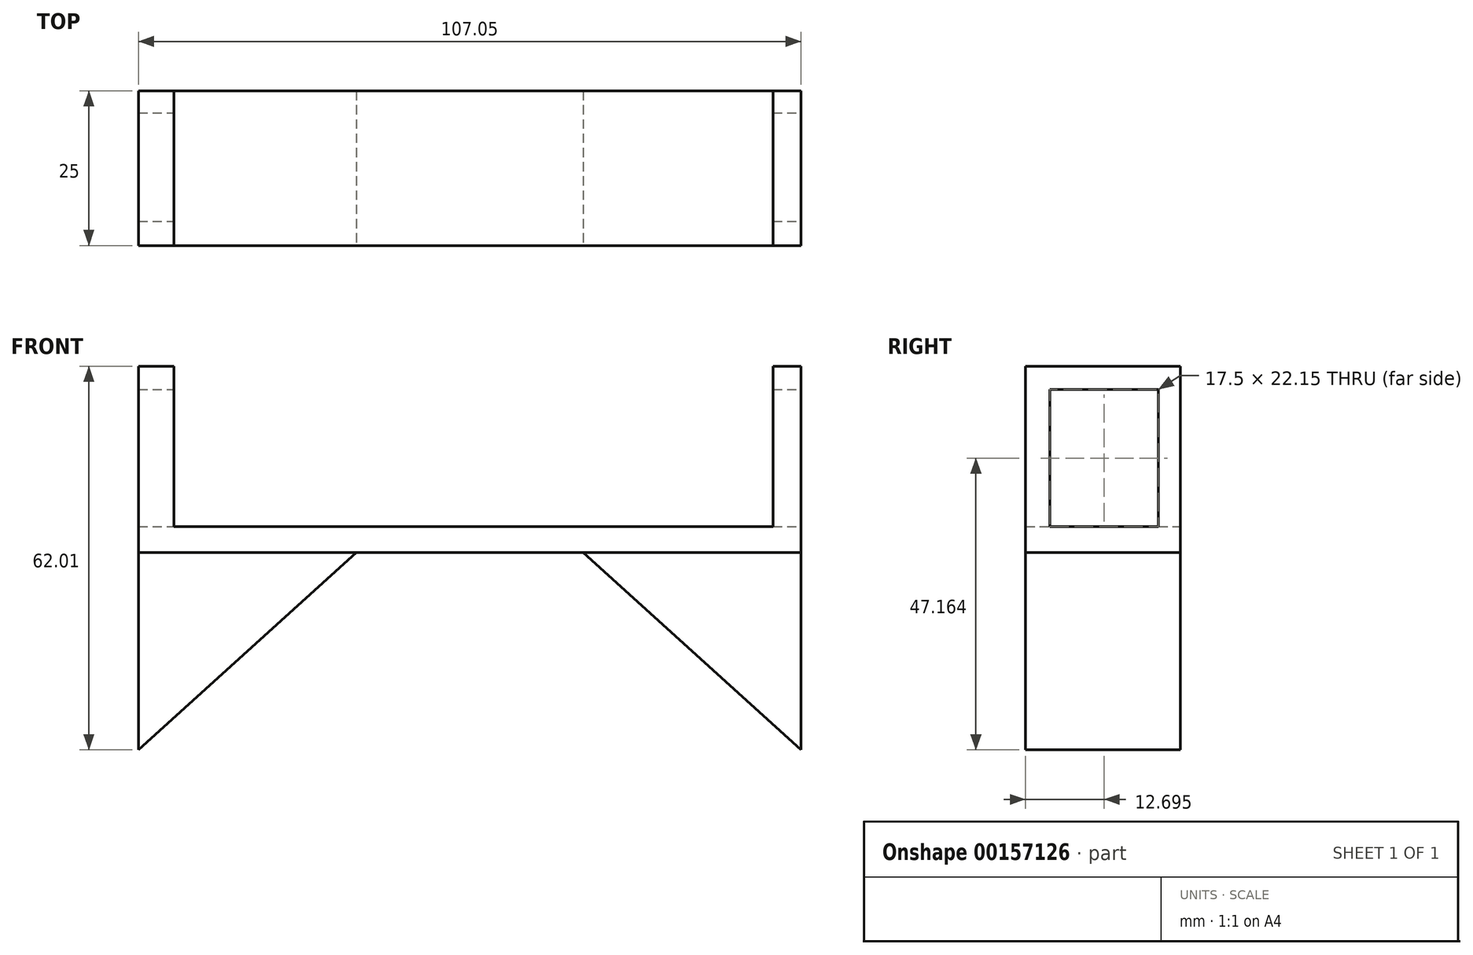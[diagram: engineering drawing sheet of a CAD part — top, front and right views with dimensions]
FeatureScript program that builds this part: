
annotation { "Feature Type Name" : "Feature", "Feature Type Description" : "" }
export const myFeature = defineFeature(function(context is Context, id is Id, definition is map)
    precondition{}
    {
        {
            var Q0;
            Q0=qCreatedBy(makeId("Front.planeOp"),FACE);
            var sketch = newSketch(context, id + "F0", { "sketchPlane" : qUnion([Q0])});
            skLineSegment(sketch, "E0", {"start": v(-62.56, 0) * mm, "end": v(44.49, 0) * mm});
            skLineSegment(sketch, "E1", {"start": v(-56.8, 0) * mm, "end": v(-56.8, 25.92) * mm});
            skLineSegment(sketch, "E2", {"start": v(-56.8, 25.92) * mm, "end": v(-62.56, 25.92) * mm});
            skLineSegment(sketch, "E3", {"start": v(-62.56, 0) * mm, "end": v(-62.56, 25.92) * mm});
            skLineSegment(sketch, "E4", {"start": v(44.49, 0) * mm, "end": v(44.49, 25.92) * mm});
            skLineSegment(sketch, "E5", {"start": v(44.49, 25.92) * mm, "end": v(39.92, 25.92) * mm});
            skLineSegment(sketch, "E6", {"start": v(39.92, 25.92) * mm, "end": v(39.92, 0) * mm});
            skLineSegment(sketch, "E7", {"start": v(-62.56, 0) * mm, "end": v(-62.56, -4.16) * mm});
            skLineSegment(sketch, "E8", {"start": v(-62.56, -4.16) * mm, "end": v(44.49, -4.16) * mm});
            skLineSegment(sketch, "E9", {"start": v(44.49, 0) * mm, "end": v(44.49, -4.16) * mm});
            skSolve(sketch);
        }
        {
            var Q0;
            Q0 = qSketchRegion(id + "F0", true);
            extrude(context, id + "F1", {"entities" : qUnion([Q0]), "depth" : 25 * mm});
        }
        {
            var Q0;
            Q0=makeQuery(id+"F1.opExtrude","SWEPT_FACE",FACE,{"disambiguationData":[OSD([sQuery(id+"F0.wireOp",EDGE,"E4"),sQuery(id+"F0.wireOp",EDGE,"E9")])]});
            var sketch = newSketch(context, id + "F2", { "sketchPlane" : qUnion([Q0])});
            skLineSegment(sketch, "E10.bottom", {"start": v(-21.05, 22.15) * mm, "end": v(-3.55, 22.15) * mm});
            skLineSegment(sketch, "E10.top", {"start": v(-21.05, 0) * mm, "end": v(-3.55, 0) * mm});
            skLineSegment(sketch, "E10.left", {"start": v(-21.05, 22.15) * mm, "end": v(-21.05, 0) * mm});
            skLineSegment(sketch, "E10.right", {"start": v(-3.55, 22.15) * mm, "end": v(-3.55, 0) * mm});
            skSolve(sketch);
        }
        {
            var Q0;
            Q0 = qSketchRegion(id + "F2", true);
            extrude(context, id + "F3", {"entities" : qUnion([Q0]), "operationType" : NewBodyOperationType.REMOVE, "endBound" : BoundingType.THROUGH_ALL, "oppositeDirection" : true, "depth" : 25 * mm});
        }
        {
            var Q0;
            Q0=makeQuery(id+"F1.opExtrude","CAP_FACE",FACE,{"disambiguationData":[OSD([sQuery(id+"F0.wireOp",EDGE,"E0"),sQuery(id+"F0.wireOp",EDGE,"E1"),sQuery(id+"F0.wireOp",EDGE,"E2"),sQuery(id+"F0.wireOp",EDGE,"E3"),sQuery(id+"F0.wireOp",EDGE,"E4"),sQuery(id+"F0.wireOp",EDGE,"E5"),sQuery(id+"F0.wireOp",EDGE,"E6"),sQuery(id+"F0.wireOp",EDGE,"E7"),sQuery(id+"F0.wireOp",EDGE,"E8"),sQuery(id+"F0.wireOp",EDGE,"E9")])],"isStart":false});
            var sketch = newSketch(context, id + "F4", { "sketchPlane" : qUnion([Q0])});
            skLineSegment(sketch, "E11", {"start": v(-62.56, -4.16) * mm, "end": v(-62.56, -36.1) * mm});
            skLineSegment(sketch, "E12", {"start": v(-62.56, -36.1) * mm, "end": v(-27.34, -4.16) * mm});
            skLineSegment(sketch, "E13", {"start": v(44.49, -4.16) * mm, "end": v(9.27, -4.16) * mm});
            skLineSegment(sketch, "E14", {"start": v(44.49, -4.16) * mm, "end": v(44.49, -36.1) * mm});
            skLineSegment(sketch, "E15", {"start": v(44.49, -36.1) * mm, "end": v(9.27, -4.16) * mm});
            skSolve(sketch);
        }
        {
            var Q0;
            Q0=makeQuery(id+"F4.imprint","IMPRINT",FACE,{"disambiguationData":[TD([[makeQuery(id+"F4.imprint","IMPRINT",EDGE,{"derivedFrom":sQuery(id+"F4.wireOp",EDGE,"E13")}),-1.0]])]});
            extrude(context, id + "F5", {"entities" : qUnion([Q0]), "oppositeDirection" : true, "depth" : 25 * mm});
        }
        {
            var Q0;
            {var subQ0=sQuery(id+"F4.wireOp",EDGE,"E11");Q0=makeQuery(id+"F4.imprint","IMPRINT",FACE,{"disambiguationData":[TD([[makeQuery(id+"F4.imprint","IMPRINT",EDGE,{"derivedFrom":subQ0}),1.0]])]});}
            extrude(context, id + "F6", {"entities" : qUnion([Q0]), "oppositeDirection" : true, "depth" : 25 * mm});
        }
    });
